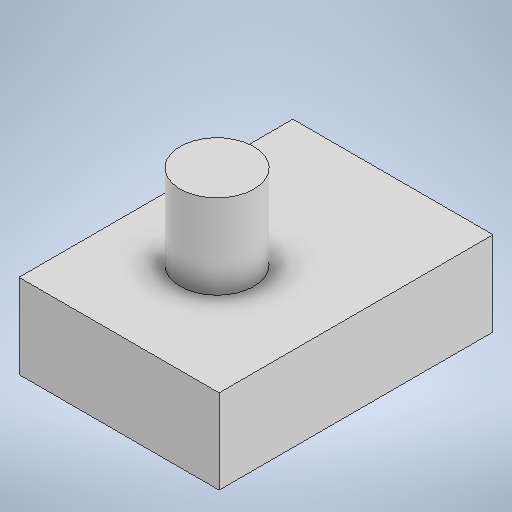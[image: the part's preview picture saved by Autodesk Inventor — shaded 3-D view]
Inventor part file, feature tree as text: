
AUTODESK INVENTOR PART (.ipt)
format: ipt  version: 2025.1 (Build 291241000, 241)  size: 205,312 bytes
history: native  units: mm
features: extrude x2, sketch x2
ambient origin geometry x8: Origin, YZ Plane, XZ Plane, XY Plane, X Axis, Y Axis, Z Axis, Center Point
bodies: Volumenkörper1 (feature_tree)
feature tree (4):
  extrude  "Extrusion1"  Depth=26.0mm
  extrude  "Extrusion2"  Depth=8.0mm
  sketch  "Skizze1"  dims[d0=19.0mm d1=26.0mm]
  sketch  "Skizze2"  dims[d2=8.0mm d3=0.0mm d4=7.0mm d5=10.4mm d6=8.4mm d7=8.0mm d8=0.0mm]
